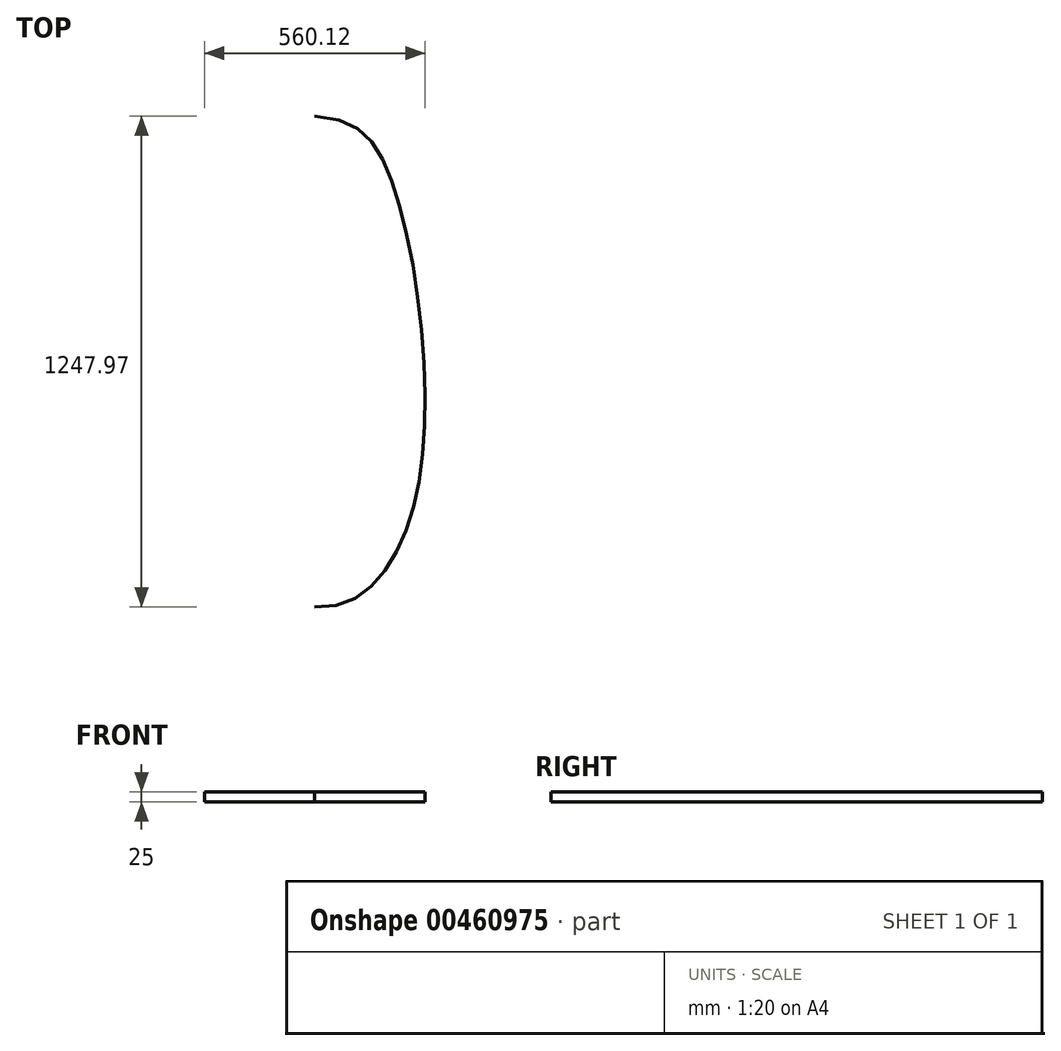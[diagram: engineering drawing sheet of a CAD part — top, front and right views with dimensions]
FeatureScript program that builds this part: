
annotation { "Feature Type Name" : "Feature", "Feature Type Description" : "" }
export const myFeature = defineFeature(function(context is Context, id is Id, definition is map)
    precondition{}
    {
        {
            var Q0;
            Q0=qCreatedBy(makeId("Top.planeOp"),FACE);
            var sketch = newSketch(context, id + "F0", { "sketchPlane" : qUnion([Q0])});
            skFitSpline(sketch, "E0", {"points": [v(0, 714.62) * mm, v(-190, 564) * mm, v(-280, 0) * mm, v(-200.17, -407.23) * mm, v(0, -532.64) * mm], "startDerivative": vector(-1610.98, -94.52) * mm, "endDerivative": vector(1333.2, 113.08) * mm});
            skFitSpline(sketch, "E1.MirrorCS", {"points": [v(0, 714.62) * mm, v(190, 564) * mm, v(280, 0) * mm, v(200.17, -407.23) * mm, v(0, -532.64) * mm], "startDerivative": vector(1610.98, -94.52) * mm, "endDerivative": vector(-1333.2, 113.08) * mm});
            skFitSpline(sketch, "E2.MirrorCS", {"points": [v(0, 714.62) * mm, v(190, 564) * mm, v(280, 0) * mm, v(200.17, -407.23) * mm, v(0, -532.64) * mm], "startDerivative": vector(1610.98, -94.52) * mm, "endDerivative": vector(-1333.2, 113.08) * mm});
            skSolve(sketch);
        }
        {
            var Q0;
            Q0 = qSketchRegion(id + "F0", true);
            extrude(context, id + "F1", {"entities" : qUnion([Q0]), "depth" : 25 * mm});
        }
    });
